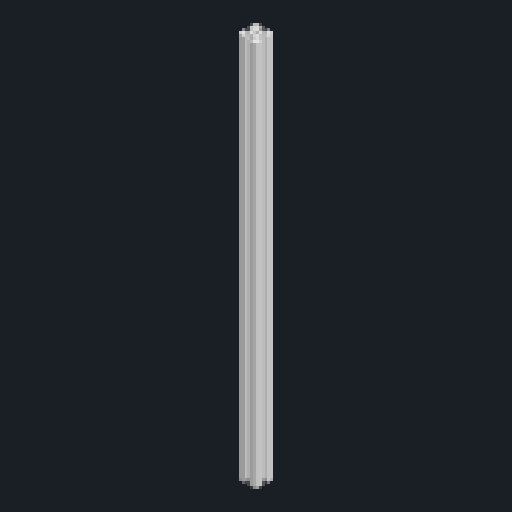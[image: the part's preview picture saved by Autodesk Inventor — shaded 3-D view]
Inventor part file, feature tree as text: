
AUTODESK INVENTOR PART (.ipt)
format: ipt  version: 2023.1 (Build 271208000, 208)  size: 140,800 bytes
history: native  units: mm
features: extrude x2, sketch x1, pattern_circular x1, fillet x1
ambient origin geometry x8: Origin, YZ Plane, XZ Plane, XY Plane, X Axis, Y Axis, Z Axis, Center Point
bodies: Solid1 (feature_tree)
feature tree (5):
  sketch  "Sketch1"  dims[d0=4.3mm d1=20.0mm d2=20.0mm d3=5.0mm d4=6.4mm d5=420.0mm d6=0.0mm d7=420.0mm d8=0.0mm d9=40.0mm d10=360.0deg d14=11.5mm d15=2.0mm]
  extrude  "Extrusion1"  Depth=20.0mm
  extrude  "Extrusion2"  Depth=20.0mm
  pattern_circular  "Circular Pattern1"  [2 undecoded]
  fillet  "Fillet1"  Radius=6.4mm
note: 2 required parameter values undecoded (feature->parameter linkage not recoverable at this tier; creation-order binding heuristic only, values carry confidence <= 0.55)
